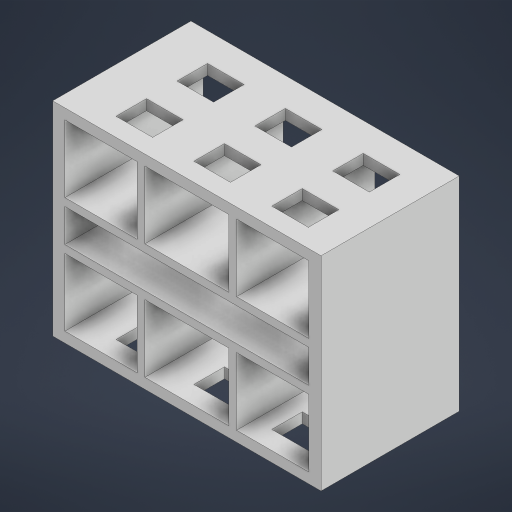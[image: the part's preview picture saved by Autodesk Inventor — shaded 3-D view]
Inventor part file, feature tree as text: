
AUTODESK INVENTOR PART (.ipt)
format: ipt  version: 2024.3 (Build 283343000, 343)  size: 310,784 bytes
history: native  units: mm
features: extrude x3, sketch x3
ambient origin geometry x8: Origin, YZ Plane, XZ Plane, XY Plane, X Axis, Y Axis, Z Axis, Center Point
bodies: Solid1 (feature_tree)
feature tree (6):
  extrude  "Extrusion1"  Depth=9000.0mm
  extrude  "Extrusion2"  Depth=10020.0mm
  extrude  "Extrusion4"  Depth=1800.0mm
  sketch  "Sketch1"  dims[d0=12000.0mm d1=9000.0mm]
  sketch  "Sketch2"  dims[d2=13200.0mm d3=10020.0mm]
  sketch  "Sketch3"  dims[d4=6800.0mm d5=0.0mm d6=1800.0mm d7=1500.0mm d8=1525.0mm d9=1400.0mm d10=1800.0mm d11=1500.0mm d12=1500.0mm d13=1525.0mm d14=1800.0mm d15=1500.0mm d16=1800.0mm d17=1500.0mm d18=1500.0mm d19=1800.0mm d20=1500.0mm d21=1800.0mm d22=1500.0mm d23=1500.0mm d24=2030.0mm d25=2030.0mm d26=11000.0mm d27=0.0mm d32=90.0deg d39=3310.0mm d46=3555.0mm d47=380.0mm d50=380.0mm d52=3555.0mm d53=0.0mm d54=0.0mm d55=6800.0mm d56=0.0mm d28=0.5mm d29=0.872665mm]
